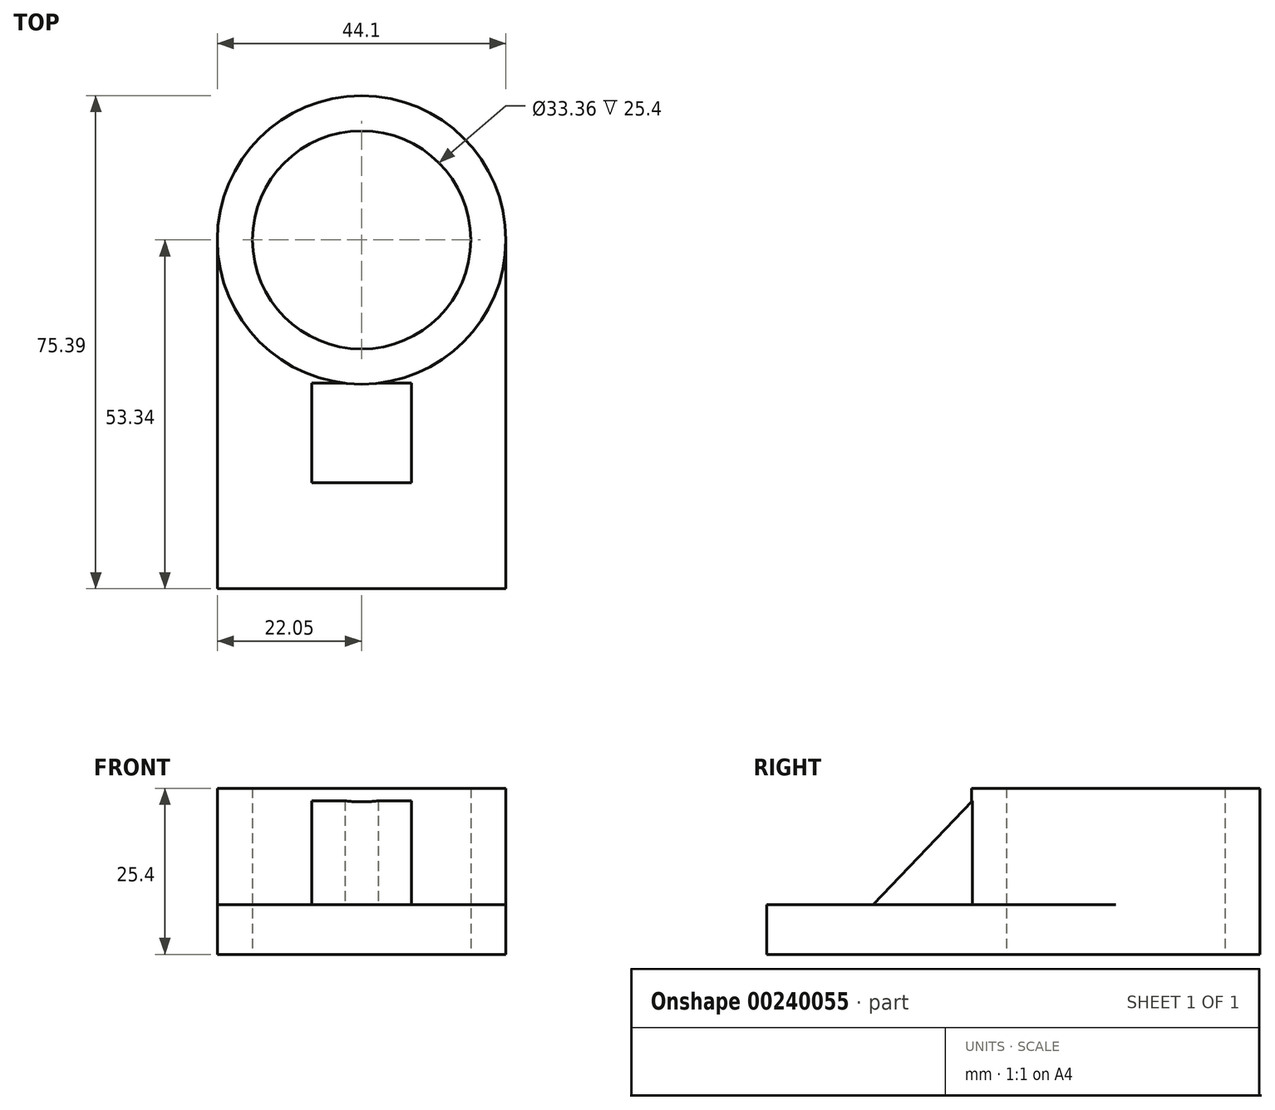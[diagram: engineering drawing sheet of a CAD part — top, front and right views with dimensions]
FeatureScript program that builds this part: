
annotation { "Feature Type Name" : "Feature", "Feature Type Description" : "" }
export const myFeature = defineFeature(function(context is Context, id is Id, definition is map)
    precondition{}
    {
        {
            var Q0;
            Q0=qCreatedBy(makeId("Top.planeOp"),FACE);
            var sketch = newSketch(context, id + "F0", { "sketchPlane" : qUnion([Q0])});
            skPoint(sketch, "E0.middle", {"position": v(0, 0) * mm});
            skCircle(sketch, "E1", {"center": v(0, 37.1) * mm, "radius": 22.05 * mm});
            skCircle(sketch, "E2", {"center": v(0, 37.1) * mm, "radius": 16.68 * mm});
            skLineSegment(sketch, "E3", {"start": v(-22.05, 37.1) * mm, "end": v(-22.05, -16.24) * mm});
            skLineSegment(sketch, "E4", {"start": v(22.05, 37.1) * mm, "end": v(22.05, -16.24) * mm});
            skLineSegment(sketch, "E5", {"start": v(22.05, -16.24) * mm, "end": v(-22.05, -16.24) * mm});
            skSolve(sketch);
        }
        {
            var Q0;
            {var subQ0=sQuery(id+"F0.wireOp",EDGE,"E3");Q0=makeQuery(id+"F0.imprint","IMPRINT",FACE,{"disambiguationData":[TD([[makeQuery(id+"F0.imprint","IMPRINT",EDGE,{"derivedFrom":subQ0}),1.0]])]});}
            extrude(context, id + "F1", {"entities" : qUnion([Q0]), "depth" : 7.62 * mm});
        }
        {
            var Q0;
            Q0=makeQuery(id+"F0.imprint","IMPRINT",FACE,{"disambiguationData":[TD([[makeQuery(id+"F0.imprint","IMPRINT",EDGE,{"derivedFrom":sQuery(id+"F0.wireOp",EDGE,"E2")}),-1.0]])]});
            extrude(context, id + "F2", {"entities" : qUnion([Q0]), "operationType" : NewBodyOperationType.ADD, "depth" : 25.4 * mm});
        }
        {
            var Q0;
            Q0=qCreatedBy(makeId("Right.planeOp"),FACE);
            var sketch = newSketch(context, id + "F3", { "sketchPlane" : qUnion([Q0])});
            skLineSegment(sketch, "E6", {"start": v(0, 0) * mm, "end": v(0, 7.62) * mm, "construction": true});
            skLineSegment(sketch, "E7", {"start": v(0, 7.62) * mm, "end": v(15.2, 7.62) * mm});
            skLineSegment(sketch, "E8", {"start": v(15.2, 7.62) * mm, "end": v(15.2, 23.47) * mm});
            skLineSegment(sketch, "E9", {"start": v(15.2, 23.47) * mm, "end": v(0, 7.62) * mm});
            skSolve(sketch);
        }
        {
            var Q0;
            Q0=makeQuery(id+"F3.imprint","IMPRINT",FACE,{"disambiguationData":[TD([[makeQuery(id+"F3.imprint","IMPRINT",EDGE,{"derivedFrom":sQuery(id+"F3.wireOp",EDGE,"E7")}),1.0]])]});
            extrude(context, id + "F4", {"entities" : qUnion([Q0]), "operationType" : NewBodyOperationType.ADD, "depth" : 7.62 * mm, "hasSecondDirection" : true, "secondDirectionOppositeDirection" : true, "secondDirectionDepth" : 7.62 * mm});
        }
    });
